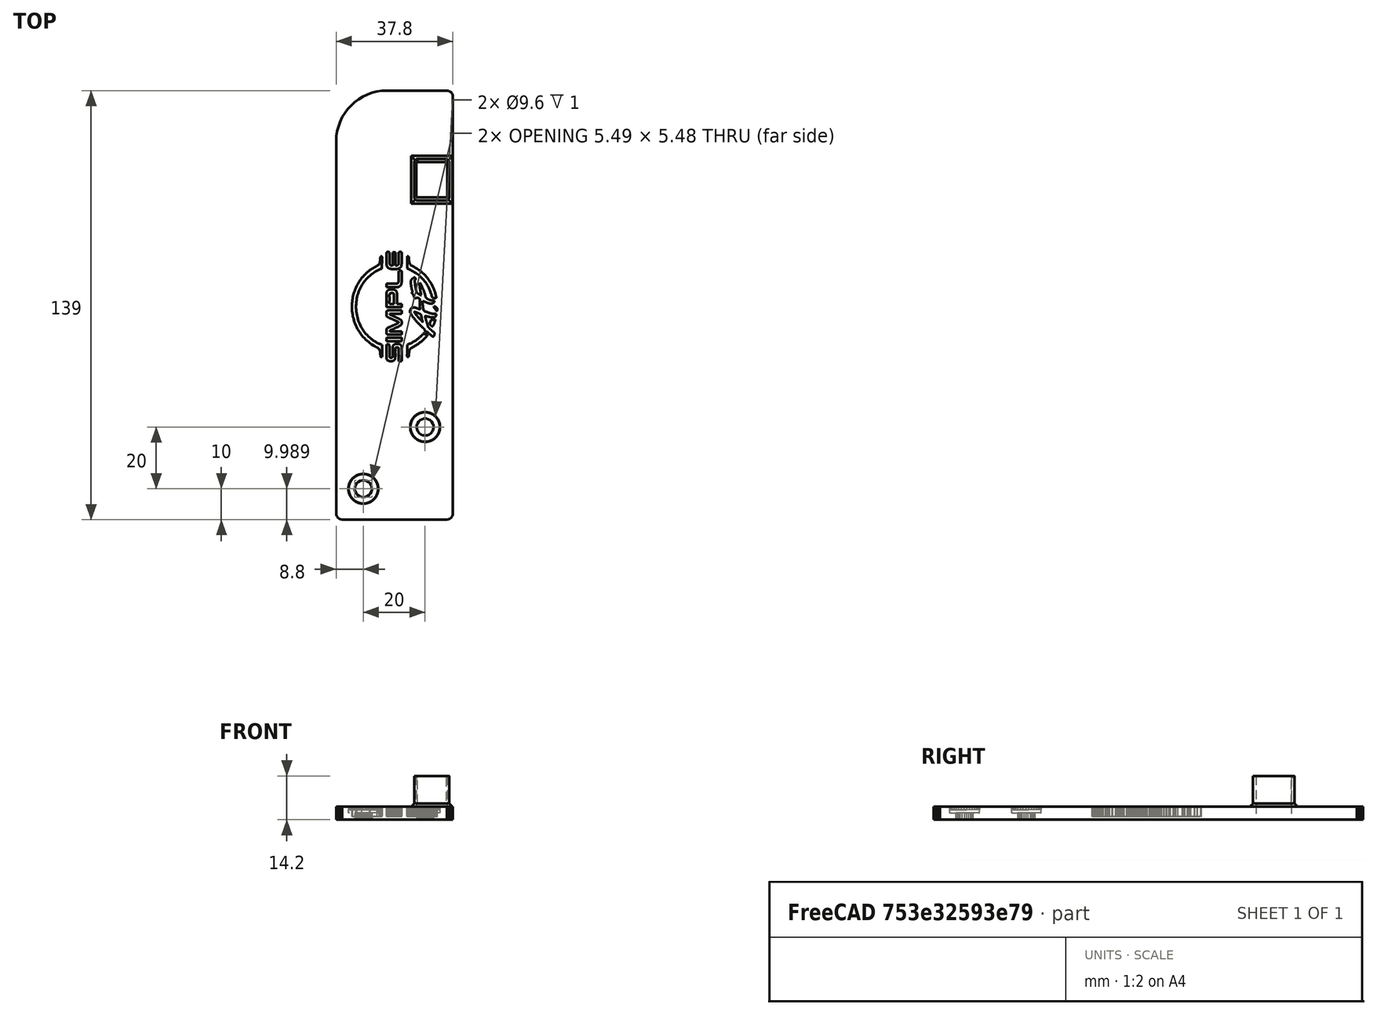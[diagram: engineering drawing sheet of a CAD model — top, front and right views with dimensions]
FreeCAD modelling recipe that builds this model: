
FCSTD DOCUMENT  (FreeCAD 1.1R44555 (Git))
Label: Ender3USBSupport
License: All rights reserved
LicenseURL: https://en.wikipedia.org/wiki/All_rights_reserved
objects: Sketcher::SketchObject×10, PartDesign::Pocket×6, PartDesign::Pad×5, PartDesign::SubShapeBinder×3, Part::Feature×2, PartDesign::Chamfer×2, Mesh::Feature×1, Part::Refine×1, App::Point×1, PartDesign::FeatureBase×1, PartDesign::Fillet×1, PartDesign::Body×1
note: 71 computed .brp shape members not serialized (recipe doc carries the construction recipe); baked Part::Feature solids carry a one-line shape summary decoded from their .brp

FEATURE [Mesh::Feature] House
FEATURE [Part::Feature] House001
  shape: bbox 37.8 x 139 x 16.2 mm, 1878 faces, 0 solids (baked)
FEATURE [Part::Refine] House002
  Source = -> House001
FEATURE [Part::Feature] House002_solid  label="House002 (Solid)"
  shape: bbox 37.8 x 139 x 16.2 mm, 936 faces (baked)
FEATURE [App::Point] Origin001
  Role = Origin
FEATURE [PartDesign::FeatureBase] BaseFeature
  BaseFeature = -> House002_solid
  Suppressed = false
FEATURE [Sketcher::SketchObject] Sketch
  ArcFitTolerance = 1e-06
  AttachmentSupport = -> [BaseFeature]
  ExternalTypes = [0]
  FullyConstrained = false
  MakeInternals = false
  MapMode = 5
  Placement = pos=(0,0,16.1903) rot=(0,0,1;0rad)
  sketch-geometry (4):
    g0: LineSegment StartX=26.4364 StartY=143.827 StartZ=0 EndX=26.4364 EndY=37.4239 EndZ=0
    g1: LineSegment StartX=26.4364 StartY=37.4239 StartZ=0 EndX=73.2674 EndY=37.4239 EndZ=0
    g2: LineSegment StartX=73.2674 StartY=37.4239 StartZ=0 EndX=73.2674 EndY=143.827 EndZ=0
    g3: LineSegment StartX=73.2674 StartY=143.827 StartZ=0 EndX=26.4364 EndY=143.827 EndZ=0
  constraints (8):
    c: Coincident(g0,g1)
    c: Coincident(g1,g2)
    c: Coincident(g2,g3)
    c: Coincident(g3,g0)
    c: Vertical(g0)
    c: Vertical(g2)
    c: Horizontal(g1)
    c: Horizontal(g3)
FEATURE [PartDesign::Pocket] Pocket
  BaseFeature = -> BaseFeature
  Direction = (0,0,-1)
  Length = 5
  Length2 = 5
  Profile = -> Sketch
  ReferenceAxis = -> Sketch [N_Axis]
  Refine = true
  SideType = 0
  Suppressed = false
  Type = 3
  Type2 = 0
  UpToFace = -> BaseFeature [Face370]
FEATURE [PartDesign::SubShapeBinder] Binder
  BindCopyOnChange = 0
  BindMode = 0
  ClaimChildren = false
  Context = -> Body [Binder.]
  Fuse = false
  MakeFace = true
  OffsetFill = false
  OffsetIntersection = false
  OffsetJoinType = 0
  OffsetOpenResult = false
  PartialLoad = false
  Refine = true
  Relative = true
  Support = -> [Pocket[Face177]]
  _Version = 2
FEATURE [PartDesign::Pad] Pad
  BaseFeature = -> Pocket
  Direction = (0,0,-1)
  Length = 10
  Length2 = 10
  Profile = -> Binder
  Refine = true
  SideType = 0
  Suppressed = false
  Type = 3
  Type2 = 0
  UpToFace = -> Pocket [Face86]
FEATURE [Sketcher::SketchObject] Sketch001
  ArcFitTolerance = 1e-06
  AttachmentSupport = -> [Pad]
  ExternalGeometry = -> [Pad]
  ExternalTypes = [0,0,0,0,0,0,0,0,0]
  FullyConstrained = false
  MakeInternals = false
  MapMode = 5
  Placement = pos=(0,0,2.19031) rot=(0,0,1;0rad)
  sketch-geometry (10):
    g0: LineSegment StartX=68.7903 StartY=103.4 StartZ=0 EndX=57.4903 EndY=103.4 EndZ=0
    g1: LineSegment StartX=57.4903 StartY=103.4 StartZ=0 EndX=57.4903 EndY=116.8 EndZ=0
    g2: LineSegment StartX=57.4903 StartY=116.8 StartZ=0 EndX=62.8903 EndY=116.8 EndZ=0
    g3: LineSegment StartX=62.8903 StartY=115.6 StartZ=0 EndX=58.6903 EndY=115.6 EndZ=0
    g4: LineSegment StartX=58.6903 StartY=115.6 StartZ=0 EndX=58.6903 EndY=104.6 EndZ=0
    g5: LineSegment StartX=58.6903 StartY=104.6 StartZ=0 EndX=66.6903 EndY=104.6 EndZ=0
    g6: LineSegment StartX=66.6903 StartY=104.6 StartZ=0 EndX=66.6903 EndY=115.6 EndZ=0
    g7: LineSegment StartX=66.6903 StartY=115.6 StartZ=0 EndX=62.8903 EndY=115.6 EndZ=0
    g8: LineSegment StartX=62.8903 StartY=116.8 StartZ=0 EndX=68.7903 EndY=116.8 EndZ=0
    g9: LineSegment StartX=68.7903 StartY=116.8 StartZ=0 EndX=68.7903 EndY=103.4 EndZ=0
  constraints (18):
    c: Coincident(g-5,g0)
    c: Coincident(g0,g-5)
    c: Coincident(g0,g1)
    c: Coincident(g1,g-11)
    c: Coincident(g1,g2)
    c: Coincident(g3,g-8)
    c: Coincident(g3,g4)
    c: Coincident(g4,g-7)
    c: Coincident(g4,g5)
    c: Coincident(g5,g-10)
    c: Coincident(g5,g6)
    c: Coincident(g6,g-10)
    c: Coincident(g6,g7)
    c: Coincident(g8,g-4)
    c: Coincident(g8,g9)
    c: Coincident(g9,g0)
    c: Coincident(g2,g8)
    c: Coincident(g3,g7)
FEATURE [PartDesign::Pad] Pad001
  BaseFeature = -> Pad
  Direction = (0,0,1)
  Length = 10
  Length2 = 10
  Profile = -> Sketch001
  ReferenceAxis = -> Sketch001 [N_Axis]
  Refine = true
  SideType = 0
  Suppressed = false
  Type = 0
  Type2 = 0
FEATURE [Sketcher::SketchObject] Sketch002
  ArcFitTolerance = 1e-06
  AttachmentSupport = -> [Pad001]
  ExternalGeometry = -> [Pad001]
  ExternalTypes = [0,0,0,0,0,0,0,0,0]
  FullyConstrained = true
  MakeInternals = false
  MapMode = 5
  Placement = pos=(0,0,2.19031) rot=(0,0,1;0rad)
  sketch-geometry (8):
    g0: LineSegment StartX=68.7903 StartY=73 StartZ=0 EndX=43.3903 EndY=73 EndZ=0
    g1: LineSegment StartX=43.3903 StartY=73 StartZ=0 EndX=43.3903 EndY=137.8 EndZ=0
    g2: LineSegment StartX=43.3903 StartY=137.8 StartZ=0 EndX=68.7903 EndY=137.8 EndZ=0
    g3: LineSegment StartX=68.7903 StartY=137.8 StartZ=0 EndX=68.7903 EndY=116.8 EndZ=0
    g4: LineSegment StartX=68.7903 StartY=116.8 StartZ=0 EndX=57.4903 EndY=116.8 EndZ=0
    g5: LineSegment StartX=57.4903 StartY=116.8 StartZ=0 EndX=57.4903 EndY=103.4 EndZ=0
    g6: LineSegment StartX=68.7903 StartY=103.4 StartZ=0 EndX=68.7903 EndY=73 EndZ=0
    g7: LineSegment StartX=57.4903 StartY=103.4 StartZ=0 EndX=68.7903 EndY=103.4 EndZ=0
  constraints (18):
    c: Coincident(g0,g-4)
    c: Horizontal(g0)
    c: Coincident(g0,g1)
    c: Coincident(g1,g-5)
    c: Vertical(g1)
    c: Coincident(g1,g2)
    c: Horizontal(g2)
    c: Coincident(g2,g3)
    c: Coincident(g3,g-11)
    c: Vertical(g3)
    c: Coincident(g3,g4)
    c: Coincident(g4,g-10)
    c: Coincident(g4,g5)
    c: Coincident(g6,g0)
    c: Coincident(g7,g-8)
    c: Coincident(g7,g-9)
    c: Coincident(g6,g7)
    c: Coincident(g5,g7)
FEATURE [PartDesign::Pad] Pad002
  BaseFeature = -> Pad001
  Direction = (0,0,1)
  Length = 10
  Length2 = 10
  Profile = -> Sketch002
  ReferenceAxis = -> Sketch002 [N_Axis]
  Refine = true
  Reversed = true
  SideType = 0
  Suppressed = false
  Type = 3
  Type2 = 0
  UpToFace = -> Pad001 [Face134]
FEATURE [PartDesign::SubShapeBinder] Binder001
  BindCopyOnChange = 0
  BindMode = 0
  ClaimChildren = false
  Context = -> Body [Binder001.]
  Fuse = false
  MakeFace = true
  OffsetFill = false
  OffsetIntersection = false
  OffsetJoinType = 0
  OffsetOpenResult = false
  PartialLoad = false
  Refine = true
  Relative = true
  Support = -> [Pad002[Face165]]
  _Version = 2
FEATURE [PartDesign::Pad] Pad003
  BaseFeature = -> Pad002
  Direction = (0,0,-1)
  Length = 10
  Length2 = 10
  Profile = -> Binder001
  Refine = true
  SideType = 0
  Suppressed = false
  Type = 3
  Type2 = 0
  UpToFace = -> Pad002 [Face125]
FEATURE [PartDesign::Chamfer] Chamfer
  Angle = 45
  Base = -> Pad003 [Edge87,Edge88,Edge86]
  BaseFeature = -> Pad003
  ChamferType = 0
  FlipDirection = false
  Refine = true
  Size = 1
  Size2 = 1
  SupportTransform = false
  Suppressed = false
  UseAllEdges = false
FEATURE [PartDesign::Chamfer] Chamfer001
  Angle = 45
  Base = -> Chamfer [Edge2]
  BaseFeature = -> Chamfer
  ChamferType = 0
  FlipDirection = false
  Refine = true
  Size = 1
  Size2 = 1
  SupportTransform = false
  Suppressed = false
  UseAllEdges = false
FEATURE [PartDesign::Fillet] Fillet
  Base = -> Chamfer001 [Edge298,Edge294,Edge300,Edge296]
  BaseFeature = -> Chamfer001
  Radius = 1
  Refine = true
  SupportTransform = false
  Suppressed = false
  UseAllEdges = false
FEATURE [Sketcher::SketchObject] Sketch003
  ArcFitTolerance = 1e-06
  AttachmentSupport = -> [Fillet]
  ExternalGeometry = -> [Fillet]
  ExternalTypes = [0,0,0,0,0]
  FullyConstrained = true
  MakeInternals = false
  MapMode = 5
  Placement = pos=(0,0,2.19031) rot=(0,0,1;0rad)
  sketch-geometry (4):
    g0: LineSegment StartX=61.4903 StartY=132.8 StartZ=0 EndX=61.4903 EndY=119.3 EndZ=0
    g1: LineSegment StartX=61.4903 StartY=119.3 StartZ=0 EndX=64.4903 EndY=119.3 EndZ=0
    g2: LineSegment StartX=64.4903 StartY=119.3 StartZ=0 EndX=64.4903 EndY=132.8 EndZ=0
    g3: LineSegment StartX=64.4903 StartY=132.8 StartZ=0 EndX=61.4903 EndY=132.8 EndZ=0
  constraints (12):
    c: Coincident(g0,g1)
    c: Coincident(g1,g2)
    c: Coincident(g2,g3)
    c: Coincident(g3,g0)
    c: Vertical(g0)
    c: Vertical(g2)
    c: Horizontal(g1)
    c: Horizontal(g3)
    c: DistanceY(g2,g2) = 13.5
    c: DistanceY(g-3,g0) = 1.5
    c: Distance(g1,g1) = 3
    c: Distance(g1,g-7) = 5.5
FEATURE [Sketcher::SketchObject] Sketch006
  ArcFitTolerance = 1e-06
  ExternalTypes = [0,0]
  FullyConstrained = false
  MakeInternals = false
  MapMode = 5
  Placement = pos=(0,0,2.19031) rot=(0,0,1;0rad)
  sketch-geometry (3):
    g0: ArcOfCircle CenterX=48.6683 CenterY=122.522 CenterZ=0 NormalX=0 NormalY=0 NormalZ=1 AngleXU=0 Radius=16.478 StartAngle=1.5708 EndAngle=3.14159
    g1: LineSegment StartX=32.1903 StartY=122.522 StartZ=0 EndX=32.083 EndY=139 EndZ=0
    g2: LineSegment StartX=32.083 StartY=139 StartZ=0 EndX=48.6683 EndY=139 EndZ=0
  constraints (6):
    c: Coincident(g0,g1)
    c: Coincident(g1,g2)
    c: Coincident(g2,g0)
    c: Horizontal(g2)
    c: Tangent(g0,g-4) = -1.5708
    c: Tangent(g0,g-3) = 1.5708
FEATURE [PartDesign::Pocket] Pocket004
  BaseFeature = -> Fillet
  Direction = (0,0,-1)
  Length = 5
  Length2 = 5
  Profile = -> Sketch006
  ReferenceAxis = -> Sketch006 [N_Axis]
  Refine = true
  SideType = 0
  Suppressed = false
  Type = 0
  Type2 = 0
FEATURE [PartDesign::SubShapeBinder] Binder002
  BindCopyOnChange = 0
  BindMode = 0
  ClaimChildren = false
  Context = -> Body [Binder002.]
  Fuse = false
  MakeFace = true
  OffsetFill = false
  OffsetIntersection = false
  OffsetJoinType = 0
  OffsetOpenResult = false
  PartialLoad = false
  Refine = true
  Relative = true
  Support = -> [Pocket004[Face108]]
  _Version = 2
FEATURE [PartDesign::Pad] Pad004
  BaseFeature = -> Pocket004
  Direction = (0,0,-1)
  Length = 2
  Length2 = 10
  Profile = -> Binder002
  Refine = true
  SideType = 0
  Suppressed = false
  Type = 0
  Type2 = 0
FEATURE [Sketcher::SketchObject] Sketch004
  ArcFitTolerance = 1e-06
  AttachmentOffset = pos=(37,87,0) rot=(0,0,1;0rad)
  AttachmentSupport = -> [Pad004]
  ExternalTypes = [0]
  FullyConstrained = false
  MakeInternals = false
  MapMode = 5
  Placement = pos=(37,87,2.19031) rot=(0,0,1;0rad)
  sketch-geometry (160):
    g0: BSplineCurve PolesCount=4 KnotsCount=2 Degree=3 IsPeriodic=0
    g1: BSplineCurve PolesCount=4 KnotsCount=2 Degree=3 IsPeriodic=0
    g2: BSplineCurve PolesCount=4 KnotsCount=2 Degree=3 IsPeriodic=0
    g3: BSplineCurve PolesCount=4 KnotsCount=2 Degree=3 IsPeriodic=0
    g4: BSplineCurve PolesCount=4 KnotsCount=2 Degree=3 IsPeriodic=0
    g5: BSplineCurve PolesCount=4 KnotsCount=2 Degree=3 IsPeriodic=0
    g6: BSplineCurve PolesCount=4 KnotsCount=2 Degree=3 IsPeriodic=0
    g7: BSplineCurve PolesCount=4 KnotsCount=2 Degree=3 IsPeriodic=0
    g8: BSplineCurve PolesCount=4 KnotsCount=2 Degree=3 IsPeriodic=0
    g9: BSplineCurve PolesCount=4 KnotsCount=2 Degree=3 IsPeriodic=0
    g10: BSplineCurve PolesCount=4 KnotsCount=2 Degree=3 IsPeriodic=0
    g11: BSplineCurve PolesCount=4 KnotsCount=2 Degree=3 IsPeriodic=0
    g12: BSplineCurve PolesCount=4 KnotsCount=2 Degree=3 IsPeriodic=0
    g13: BSplineCurve PolesCount=4 KnotsCount=2 Degree=3 IsPeriodic=0
    g14: BSplineCurve PolesCount=4 KnotsCount=2 Degree=3 IsPeriodic=0
    g15: BSplineCurve PolesCount=4 KnotsCount=2 Degree=3 IsPeriodic=0
    g16: BSplineCurve PolesCount=4 KnotsCount=2 Degree=3 IsPeriodic=0
    g17: BSplineCurve PolesCount=4 KnotsCount=2 Degree=3 IsPeriodic=0
    g18: BSplineCurve PolesCount=4 KnotsCount=2 Degree=3 IsPeriodic=0
    g19: BSplineCurve PolesCount=4 KnotsCount=2 Degree=3 IsPeriodic=0
    g20: BSplineCurve PolesCount=4 KnotsCount=2 Degree=3 IsPeriodic=0
    g21: BSplineCurve PolesCount=4 KnotsCount=2 Degree=3 IsPeriodic=0
    g22: BSplineCurve PolesCount=4 KnotsCount=2 Degree=3 IsPeriodic=0
    g23: BSplineCurve PolesCount=4 KnotsCount=2 Degree=3 IsPeriodic=0
    g24: BSplineCurve PolesCount=4 KnotsCount=2 Degree=3 IsPeriodic=0
    g25: BSplineCurve PolesCount=4 KnotsCount=2 Degree=3 IsPeriodic=0
    g26: BSplineCurve PolesCount=4 KnotsCount=2 Degree=3 IsPeriodic=0
    g27: BSplineCurve PolesCount=4 KnotsCount=2 Degree=3 IsPeriodic=0
    g28: BSplineCurve PolesCount=4 KnotsCount=2 Degree=3 IsPeriodic=0
    g29: BSplineCurve PolesCount=4 KnotsCount=2 Degree=3 IsPeriodic=0
    g30: BSplineCurve PolesCount=4 KnotsCount=2 Degree=3 IsPeriodic=0
    g31: BSplineCurve PolesCount=4 KnotsCount=2 Degree=3 IsPeriodic=0
    g32: BSplineCurve PolesCount=4 KnotsCount=2 Degree=3 IsPeriodic=0
    g33: BSplineCurve PolesCount=4 KnotsCount=2 Degree=3 IsPeriodic=0
    g34: BSplineCurve PolesCount=4 KnotsCount=2 Degree=3 IsPeriodic=0
    g35: BSplineCurve PolesCount=4 KnotsCount=2 Degree=3 IsPeriodic=0
    g36: BSplineCurve PolesCount=4 KnotsCount=2 Degree=3 IsPeriodic=0
    g37: BSplineCurve PolesCount=4 KnotsCount=2 Degree=3 IsPeriodic=0
    g38: BSplineCurve PolesCount=4 KnotsCount=2 Degree=3 IsPeriodic=0
    g39: BSplineCurve PolesCount=4 KnotsCount=2 Degree=3 IsPeriodic=0
    g40: BSplineCurve PolesCount=4 KnotsCount=2 Degree=3 IsPeriodic=0
    g41: BSplineCurve PolesCount=4 KnotsCount=2 Degree=3 IsPeriodic=0
    g42: BSplineCurve PolesCount=4 KnotsCount=2 Degree=3 IsPeriodic=0
    g43: BSplineCurve PolesCount=4 KnotsCount=2 Degree=3 IsPeriodic=0
    g44: BSplineCurve PolesCount=4 KnotsCount=2 Degree=3 IsPeriodic=0
    g45: BSplineCurve PolesCount=4 KnotsCount=2 Degree=3 IsPeriodic=0
    g46: BSplineCurve PolesCount=4 KnotsCount=2 Degree=3 IsPeriodic=0
    g47: BSplineCurve PolesCount=4 KnotsCount=2 Degree=3 IsPeriodic=0
    g48: BSplineCurve PolesCount=4 KnotsCount=2 Degree=3 IsPeriodic=0
    g49: BSplineCurve PolesCount=4 KnotsCount=2 Degree=3 IsPeriodic=0
    g50: BSplineCurve PolesCount=4 KnotsCount=2 Degree=3 IsPeriodic=0
    g51: BSplineCurve PolesCount=4 KnotsCount=2 Degree=3 IsPeriodic=0
    g52: BSplineCurve PolesCount=4 KnotsCount=2 Degree=3 IsPeriodic=0
    g53: BSplineCurve PolesCount=4 KnotsCount=2 Degree=3 IsPeriodic=0
    g54: BSplineCurve PolesCount=4 KnotsCount=2 Degree=3 IsPeriodic=0
    g55: BSplineCurve PolesCount=4 KnotsCount=2 Degree=3 IsPeriodic=0
    g56: BSplineCurve PolesCount=4 KnotsCount=2 Degree=3 IsPeriodic=0
    g57: BSplineCurve PolesCount=4 KnotsCount=2 Degree=3 IsPeriodic=0
    g58: BSplineCurve PolesCount=4 KnotsCount=2 Degree=3 IsPeriodic=0
    g59: BSplineCurve PolesCount=4 KnotsCount=2 Degree=3 IsPeriodic=0
    g60: BSplineCurve PolesCount=4 KnotsCount=2 Degree=3 IsPeriodic=0
    g61: BSplineCurve PolesCount=4 KnotsCount=2 Degree=3 IsPeriodic=0
    g62: BSplineCurve PolesCount=4 KnotsCount=2 Degree=3 IsPeriodic=0
    g63: BSplineCurve PolesCount=4 KnotsCount=2 Degree=3 IsPeriodic=0
    g64: BSplineCurve PolesCount=4 KnotsCount=2 Degree=3 IsPeriodic=0
    g65: BSplineCurve PolesCount=4 KnotsCount=2 Degree=3 IsPeriodic=0
    g66: BSplineCurve PolesCount=4 KnotsCount=2 Degree=3 IsPeriodic=0
    g67: BSplineCurve PolesCount=4 KnotsCount=2 Degree=3 IsPeriodic=0
    g68: BSplineCurve PolesCount=4 KnotsCount=2 Degree=3 IsPeriodic=0
    g69: BSplineCurve PolesCount=4 KnotsCount=2 Degree=3 IsPeriodic=0
    g70: BSplineCurve PolesCount=4 KnotsCount=2 Degree=3 IsPeriodic=0
    g71: BSplineCurve PolesCount=4 KnotsCount=2 Degree=3 IsPeriodic=0
    g72: BSplineCurve PolesCount=4 KnotsCount=2 Degree=3 IsPeriodic=0
    g73: BSplineCurve PolesCount=4 KnotsCount=2 Degree=3 IsPeriodic=0
    g74: BSplineCurve PolesCount=4 KnotsCount=2 Degree=3 IsPeriodic=0
    g75: BSplineCurve PolesCount=4 KnotsCount=2 Degree=3 IsPeriodic=0
    g76: BSplineCurve PolesCount=4 KnotsCount=2 Degree=3 IsPeriodic=0
    g77: BSplineCurve PolesCount=4 KnotsCount=2 Degree=3 IsPeriodic=0
    g78: BSplineCurve PolesCount=4 KnotsCount=2 Degree=3 IsPeriodic=0
    g79: BSplineCurve PolesCount=4 KnotsCount=2 Degree=3 IsPeriodic=0
    g80: BSplineCurve PolesCount=4 KnotsCount=2 Degree=3 IsPeriodic=0
    g81: BSplineCurve PolesCount=4 KnotsCount=2 Degree=3 IsPeriodic=0
    g82: BSplineCurve PolesCount=4 KnotsCount=2 Degree=3 IsPeriodic=0
    g83: BSplineCurve PolesCount=4 KnotsCount=2 Degree=3 IsPeriodic=0
    g84: BSplineCurve PolesCount=4 KnotsCount=2 Degree=3 IsPeriodic=0
    g85: BSplineCurve PolesCount=4 KnotsCount=2 Degree=3 IsPeriodic=0
    g86: BSplineCurve PolesCount=4 KnotsCount=2 Degree=3 IsPeriodic=0
    g87: BSplineCurve PolesCount=4 KnotsCount=2 Degree=3 IsPeriodic=0
    g88: BSplineCurve PolesCount=4 KnotsCount=2 Degree=3 IsPeriodic=0
    g89: BSplineCurve PolesCount=4 KnotsCount=2 Degree=3 IsPeriodic=0
    g90: BSplineCurve PolesCount=4 KnotsCount=2 Degree=3 IsPeriodic=0
    g91: BSplineCurve PolesCount=4 KnotsCount=2 Degree=3 IsPeriodic=0
    g92: BSplineCurve PolesCount=4 KnotsCount=2 Degree=3 IsPeriodic=0
    g93: BSplineCurve PolesCount=4 KnotsCount=2 Degree=3 IsPeriodic=0
    g94: BSplineCurve PolesCount=4 KnotsCount=2 Degree=3 IsPeriodic=0
    g95: BSplineCurve PolesCount=4 KnotsCount=2 Degree=3 IsPeriodic=0
    g96: BSplineCurve PolesCount=4 KnotsCount=2 Degree=3 IsPeriodic=0
    g97: BSplineCurve PolesCount=4 KnotsCount=2 Degree=3 IsPeriodic=0
    g98: BSplineCurve PolesCount=4 KnotsCount=2 Degree=3 IsPeriodic=0
    g99: BSplineCurve PolesCount=4 KnotsCount=2 Degree=3 IsPeriodic=0
    g100: BSplineCurve PolesCount=4 KnotsCount=2 Degree=3 IsPeriodic=0
    g101: BSplineCurve PolesCount=4 KnotsCount=2 Degree=3 IsPeriodic=0
    g102: BSplineCurve PolesCount=4 KnotsCount=2 Degree=3 IsPeriodic=0
    g103: BSplineCurve PolesCount=4 KnotsCount=2 Degree=3 IsPeriodic=0
    g104: BSplineCurve PolesCount=4 KnotsCount=2 Degree=3 IsPeriodic=0
    g105: BSplineCurve PolesCount=2 KnotsCount=2 Degree=1 IsPeriodic=0
    g106: BSplineCurve PolesCount=4 KnotsCount=2 Degree=3 IsPeriodic=0
    g107: BSplineCurve PolesCount=4 KnotsCount=2 Degree=3 IsPeriodic=0
    g108: BSplineCurve PolesCount=4 KnotsCount=2 Degree=3 IsPeriodic=0
    g109: BSplineCurve PolesCount=4 KnotsCount=2 Degree=3 IsPeriodic=0
    g110: BSplineCurve PolesCount=4 KnotsCount=2 Degree=3 IsPeriodic=0
    g111: BSplineCurve PolesCount=4 KnotsCount=2 Degree=3 IsPeriodic=0
    g112: BSplineCurve PolesCount=4 KnotsCount=2 Degree=3 IsPeriodic=0
    g113: BSplineCurve PolesCount=4 KnotsCount=2 Degree=3 IsPeriodic=0
    g114: BSplineCurve PolesCount=4 KnotsCount=2 Degree=3 IsPeriodic=0
    g115: BSplineCurve PolesCount=4 KnotsCount=2 Degree=3 IsPeriodic=0
    g116: BSplineCurve PolesCount=4 KnotsCount=2 Degree=3 IsPeriodic=0
    g117: BSplineCurve PolesCount=4 KnotsCount=2 Degree=3 IsPeriodic=0
    g118: BSplineCurve PolesCount=4 KnotsCount=2 Degree=3 IsPeriodic=0
    g119: BSplineCurve PolesCount=4 KnotsCount=2 Degree=3 IsPeriodic=0
    g120: BSplineCurve PolesCount=4 KnotsCount=2 Degree=3 IsPeriodic=0
    g121: BSplineCurve PolesCount=4 KnotsCount=2 Degree=3 IsPeriodic=0
    g122: BSplineCurve PolesCount=4 KnotsCount=2 Degree=3 IsPeriodic=0
    g123: BSplineCurve PolesCount=4 KnotsCount=2 Degree=3 IsPeriodic=0
    g124: BSplineCurve PolesCount=4 KnotsCount=2 Degree=3 IsPeriodic=0
    g125: BSplineCurve PolesCount=4 KnotsCount=2 Degree=3 IsPeriodic=0
    g126: BSplineCurve PolesCount=4 KnotsCount=2 Degree=3 IsPeriodic=0
    g127: BSplineCurve PolesCount=4 KnotsCount=2 Degree=3 IsPeriodic=0
    g128: BSplineCurve PolesCount=4 KnotsCount=2 Degree=3 IsPeriodic=0
    g129: BSplineCurve PolesCount=4 KnotsCount=2 Degree=3 IsPeriodic=0
    g130: BSplineCurve PolesCount=4 KnotsCount=2 Degree=3 IsPeriodic=0
    g131: BSplineCurve PolesCount=4 KnotsCount=2 Degree=3 IsPeriodic=0
    g132: BSplineCurve PolesCount=4 KnotsCount=2 Degree=3 IsPeriodic=0
    g133: BSplineCurve PolesCount=4 KnotsCount=2 Degree=3 IsPeriodic=0
    g134: BSplineCurve PolesCount=4 KnotsCount=2 Degree=3 IsPeriodic=0
    g135: BSplineCurve PolesCount=4 KnotsCount=2 Degree=3 IsPeriodic=0
    g136: BSplineCurve PolesCount=4 KnotsCount=2 Degree=3 IsPeriodic=0
    g137: BSplineCurve PolesCount=4 KnotsCount=2 Degree=3 IsPeriodic=0
    g138: BSplineCurve PolesCount=4 KnotsCount=2 Degree=3 IsPeriodic=0
    g139: BSplineCurve PolesCount=4 KnotsCount=2 Degree=3 IsPeriodic=0
    g140: BSplineCurve PolesCount=4 KnotsCount=2 Degree=3 IsPeriodic=0
    g141: BSplineCurve PolesCount=4 KnotsCount=2 Degree=3 IsPeriodic=0
    g142: BSplineCurve PolesCount=4 KnotsCount=2 Degree=3 IsPeriodic=0
    g143: BSplineCurve PolesCount=4 KnotsCount=2 Degree=3 IsPeriodic=0
    g144: BSplineCurve PolesCount=4 KnotsCount=2 Degree=3 IsPeriodic=0
    g145: BSplineCurve PolesCount=4 KnotsCount=2 Degree=3 IsPeriodic=0
    g146: BSplineCurve PolesCount=4 KnotsCount=2 Degree=3 IsPeriodic=0
    g147: BSplineCurve PolesCount=4 KnotsCount=2 Degree=3 IsPeriodic=0
    g148: BSplineCurve PolesCount=4 KnotsCount=2 Degree=3 IsPeriodic=0
    g149: BSplineCurve PolesCount=4 KnotsCount=2 Degree=3 IsPeriodic=0
    g150: BSplineCurve PolesCount=4 KnotsCount=2 Degree=3 IsPeriodic=0
    g151: BSplineCurve PolesCount=4 KnotsCount=2 Degree=3 IsPeriodic=0
    g152: BSplineCurve PolesCount=4 KnotsCount=2 Degree=3 IsPeriodic=0
    g153: BSplineCurve PolesCount=4 KnotsCount=2 Degree=3 IsPeriodic=0
    g154: BSplineCurve PolesCount=4 KnotsCount=2 Degree=3 IsPeriodic=0
    g155: BSplineCurve PolesCount=4 KnotsCount=2 Degree=3 IsPeriodic=0
    g156: BSplineCurve PolesCount=4 KnotsCount=2 Degree=3 IsPeriodic=0
    g157: BSplineCurve PolesCount=4 KnotsCount=2 Degree=3 IsPeriodic=0
    g158: BSplineCurve PolesCount=4 KnotsCount=2 Degree=3 IsPeriodic=0
    g159: BSplineCurve PolesCount=4 KnotsCount=2 Degree=3 IsPeriodic=0
  constraints (160):
    c: Coincident(g10,g11)
    c: Coincident(g4,g5)
    c: Coincident(g11,g12)
    c: Coincident(g0,g12)
    c: Coincident(g5,g6)
    c: Coincident(g9,g10)
    c: Coincident(g0,g1)
    c: Coincident(g8,g9)
    c: Coincident(g1,g2)
    c: Coincident(g3,g4)
    c: Coincident(g2,g3)
    c: Coincident(g7,g8)
    c: Coincident(g6,g7)
    c: Coincident(g79,g80)
    c: Coincident(g96,g97)
    c: Coincident(g109,g110)
    c: Coincident(g13,g26)
    c: Coincident(g110,g111)
    c: Coincident(g13,g14)
    c: Coincident(g136,g137)
    c: Coincident(g102,g103)
    c: Coincident(g82,g83)
    c: Coincident(g137,g138)
    c: Coincident(g103,g104)
    c: Coincident(g78,g79)
    c: Coincident(g83,g84)
    c: Coincident(g80,g81)
    c: Coincident(g25,g26)
    c: Coincident(g95,g96)
    c: Coincident(g108,g109)
    c: Coincident(g73,g81)
    c: Coincident(g14,g15)
    c: Coincident(g111,g112)
    c: Coincident(g127,g131)
    c: Coincident(g127,g128)
    c: Coincident(g87,g88)
    c: Coincident(g91,g92)
    c: Coincident(g112,g113)
    c: Coincident(g15,g16)
    c: Coincident(g130,g131)
    c: Coincident(g97,g98)
    c: Coincident(g88,g89)
    c: Coincident(g84,g85)
    c: Coincident(g92,g93)
    c: Coincident(g113,g114)
    c: Coincident(g16,g17)
    c: Coincident(g17,g18)
    c: Coincident(g114,g115)
    c: Coincident(g82,g100)
    c: Coincident(g129,g130)
    c: Coincident(g128,g129)
    c: Coincident(g73,g74)
    c: Coincident(g107,g108)
    c: Coincident(g135,g136)
    c: Coincident(g18,g19)
    c: Coincident(g19,g20)
    c: Coincident(g106,g107)
    c: Coincident(g24,g25)
    c: Coincident(g99,g100)
    c: Coincident(g106,g120)
    c: Coincident(g74,g75)
    c: Coincident(g75,g76)
    c: Coincident(g138,g139)
    c: Coincident(g119,g120)
    c: Coincident(g139,g140)
    c: Coincident(g132,g140)
    c: Coincident(g20,g21)
    c: Coincident(g98,g99)
    c: Coincident(g118,g119)
    c: Coincident(g132,g133)
    c: Coincident(g21,g22)
    c: Coincident(g115,g116)
    c: Coincident(g90,g91)
    c: Coincident(g89,g90)
    c: Coincident(g77,g78)
    c: Coincident(g134,g135)
    c: Coincident(g85,g86)
    c: Coincident(g86,g87)
    c: Coincident(g23,g24)
    c: Coincident(g104,g105)
    c: Coincident(g101,g102)
    c: Coincident(g94,g95)
    c: Coincident(g117,g118)
    c: Coincident(g101,g105)
    c: Coincident(g22,g23)
    c: Coincident(g93,g94)
    c: Coincident(g76,g77)
    c: Coincident(g133,g134)
    c: Coincident(g116,g117)
    c: Coincident(g148,g149)
    c: Coincident(g157,g158)
    c: Coincident(g158,g159)
    c: Coincident(g147,g148)
    c: Coincident(g146,g147)
    c: Coincident(g156,g157)
    c: Coincident(g149,g150)
    c: Coincident(g57,g58)
    c: Coincident(g155,g156)
    c: Coincident(g46,g47)
    c: Coincident(g56,g57)
    c: Coincident(g47,g48)
    c: Coincident(g48,g49)
    c: Coincident(g45,g46)
    c: Coincident(g150,g151)
    c: Coincident(g55,g56)
    c: Coincident(g49,g50)
    c: Coincident(g122,g123)
    c: Coincident(g43,g44)
    c: Coincident(g44,g45)
    c: Coincident(g54,g55)
    c: Coincident(g123,g124)
    c: Coincident(g42,g43)
    c: Coincident(g50,g51)
    c: Coincident(g124,g125)
    c: Coincident(g53,g54)
    c: Coincident(g40,g41)
    c: Coincident(g52,g53)
    c: Coincident(g51,g52)
    c: Coincident(g58,g59)
    c: Coincident(g121,g122)
    c: Coincident(g39,g40)
    c: Coincident(g41,g42)
    c: Coincident(g38,g39)
    c: Coincident(g125,g126)
    c: Coincident(g121,g126)
    c: Coincident(g32,g33)
    c: Coincident(g31,g32)
    c: Coincident(g153,g159)
    c: Coincident(g37,g38)
    c: Coincident(g59,g60)
    c: Coincident(g67,g68)
    c: Coincident(g154,g155)
    c: Coincident(g66,g67)
    c: Coincident(g36,g37)
    c: Coincident(g60,g61)
    c: Coincident(g153,g154)
    c: Coincident(g65,g66)
    c: Coincident(g68,g69)
    c: Coincident(g71,g72)
    c: Coincident(g141,g144)
    c: Coincident(g33,g34)
    c: Coincident(g64,g65)
    c: Coincident(g145,g146)
    c: Coincident(g141,g142)
    c: Coincident(g63,g64)
    c: Coincident(g145,g152)
    c: Coincident(g143,g144)
    c: Coincident(g61,g62)
    c: Coincident(g34,g35)
    c: Coincident(g29,g30)
    c: Coincident(g35,g36)
    c: Coincident(g62,g63)
    c: Coincident(g27,g30)
    c: Coincident(g69,g70)
    c: Coincident(g70,g71)
    c: Coincident(g142,g143)
    c: Coincident(g28,g29)
    c: Coincident(g151,g152)
    c: Coincident(g27,g28)
    c: Coincident(g31,g72)
FEATURE [Sketcher::SketchObject] Sketch005
  ArcFitTolerance = 1e-06
  AttachmentSupport = -> [Pad004]
  ExternalGeometry = -> [Sketch003]
  ExternalTypes = [0,0,0,0]
  FullyConstrained = true
  MakeInternals = false
  MapMode = 5
  Placement = pos=(0,0,2.19031) rot=(0,0,1;0rad)
  sketch-geometry (4):
    g0: LineSegment StartX=57.4903 StartY=133.8 StartZ=0 EndX=57.4903 EndY=118.3 EndZ=0
    g1: LineSegment StartX=57.4903 StartY=118.3 StartZ=0 EndX=68.7903 EndY=118.3 EndZ=0
    g2: LineSegment StartX=68.7903 StartY=118.3 StartZ=0 EndX=68.7903 EndY=133.8 EndZ=0
    g3: LineSegment StartX=68.7903 StartY=133.8 StartZ=0 EndX=57.4903 EndY=133.8 EndZ=0
  constraints (12):
    c: Coincident(g0,g1)
    c: Coincident(g1,g2)
    c: Coincident(g2,g3)
    c: Coincident(g3,g0)
    c: Vertical(g0)
    c: Vertical(g2)
    c: Horizontal(g1)
    c: Horizontal(g3)
    c: DistanceY(g2,g2) = 15.5
    c: DistanceY(g1,g-5) = 1
    c: DistanceX(g-4,g0) = 1
    c: DistanceX(g1,g-4) = 1
FEATURE [PartDesign::Pocket] Pocket006
  BaseFeature = -> Pad004
  Direction = (0,0,-1)
  Length = 3.2
  Length2 = 5
  Profile = -> Sketch004
  ReferenceAxis = -> Sketch004 [N_Axis]
  Refine = true
  SideType = 0
  Suppressed = false
  Type = 0
  Type2 = 0
FEATURE [Sketcher::SketchObject] Sketch007
  ArcFitTolerance = 1e-06
  AttachmentSupport = -> [Pocket006]
  ExternalGeometry = -> [Pocket006]
  ExternalTypes = [0,0,0,0,0,0]
  FullyConstrained = true
  MakeInternals = false
  MapMode = 5
  Placement = pos=(0,0,1.19031) rot=(0,0,1;0rad)
  sketch-geometry (2):
    g0: Circle CenterX=40.9903 CenterY=10 CenterZ=0 NormalX=0 NormalY=0 NormalZ=1 AngleXU=0 Radius=4.8
    g1: Circle CenterX=60.9903 CenterY=30 CenterZ=0 NormalX=0 NormalY=0 NormalZ=1 AngleXU=0 Radius=4.8
  constraints (6):
    c: PointOnObject(g-6,g0)
    c: PointOnObject(g-7,g0)
    c: PointOnObject(g-8,g0)
    c: PointOnObject(g-5,g1)
    c: PointOnObject(g-3,g1)
    c: PointOnObject(g-4,g1)
FEATURE [PartDesign::Pocket] Pocket007
  BaseFeature = -> Pocket006
  Direction = (0,0,-1)
  Length = 1
  Length2 = 5
  Profile = -> Sketch007
  ReferenceAxis = -> Sketch007 [N_Axis]
  Refine = true
  SideType = 0
  Suppressed = false
  Type = 0
  Type2 = 0
FEATURE [Sketcher::SketchObject] Sketch008
  ArcFitTolerance = 1e-06
  ExternalTypes = [0,0,0,0]
  FullyConstrained = true
  MakeInternals = false
  MapMode = 5
  Placement = pos=(0,0,12.1903) rot=(0,0,1;0rad)
  sketch-geometry (4):
    g0: LineSegment StartX=58.1903 StartY=115.8 StartZ=0 EndX=58.1903 EndY=104.4 EndZ=0
    g1: LineSegment StartX=58.1903 StartY=104.4 StartZ=0 EndX=68.1903 EndY=104.4 EndZ=0
    g2: LineSegment StartX=68.1903 StartY=104.4 StartZ=0 EndX=68.1903 EndY=115.8 EndZ=0
    g3: LineSegment StartX=68.1903 StartY=115.8 StartZ=0 EndX=58.1903 EndY=115.8 EndZ=0
  constraints (12):
    c: Coincident(g0,g1)
    c: Coincident(g1,g2)
    c: Coincident(g2,g3)
    c: Coincident(g3,g0)
    c: Vertical(g0)
    c: Vertical(g2)
    c: Horizontal(g1)
    c: Horizontal(g3)
    c: DistanceX(g1,g1) = 10
    c: DistanceY(g2,g-3) = 1
    c: DistanceY(g-4,g1) = 1
    c: Distance(g1,g-5) = 0.6
FEATURE [PartDesign::Pocket] Pocket008
  BaseFeature = -> Pocket007
  Direction = (0,0,-1)
  Length = 5
  Length2 = 5
  Profile = -> Sketch008
  ReferenceAxis = -> Sketch008 [N_Axis]
  Refine = true
  SideType = 0
  Suppressed = false
  Type = 1
  Type2 = 0
FEATURE [Sketcher::SketchObject] Sketch009
  ArcFitTolerance = 1e-06
  AttachmentSupport = -> [Pocket008]
  ExternalGeometry = -> [Pocket008]
  ExternalTypes = [0,0,0,0,0,0]
  FullyConstrained = false
  MakeInternals = false
  MapMode = 5
  Placement = pos=(0,116.8,-1.031e-13) rot=(0,0.707107,0.707107;3.14159rad)
  sketch-geometry (6):
    g0: LineSegment StartX=-67.7903 StartY=11.6925 StartZ=0 EndX=-67.7903 EndY=3.19031 EndZ=0
    g1: LineSegment StartX=-67.7903 StartY=3.19031 StartZ=0 EndX=-58.4903 EndY=3.19031 EndZ=0
    g2: LineSegment StartX=-58.4903 StartY=3.19031 StartZ=0 EndX=-58.4903 EndY=11.6379 EndZ=0
    g3: LineSegment StartX=-58.1903 StartY=12.1903 StartZ=0 EndX=-58.4903 EndY=11.6379 EndZ=0
    g4: LineSegment StartX=-68.1903 StartY=12.1903 StartZ=0 EndX=-67.7903 EndY=11.6925 EndZ=0
    g5: LineSegment StartX=-68.1903 StartY=12.1903 StartZ=0 EndX=-58.1903 EndY=12.1903 EndZ=0
  constraints (8):
    c: Coincident(g0,g1)
    c: Horizontal(g1)
    c: Vertical(g0)
    c: Coincident(g4,g-5)
    c: Coincident(g4,g0)
    c: Coincident(g5,g4)
    c: Coincident(g5,g3)
    c: Horizontal(g5)
FEATURE [PartDesign::Pocket] Pocket009
  BaseFeature = -> Pocket008
  Direction = (0,-1,2e-16)
  Length = 5
  Length2 = 5
  Profile = -> Sketch009
  ReferenceAxis = -> Sketch009 [N_Axis]
  Refine = true
  SideType = 0
  Suppressed = false
  Type = 0
  Type2 = 0
FEATURE [PartDesign::Body] Body
  AllowCompound = true
  BaseFeature = -> House002_solid
  Group = -> [BaseFeature,Sketch,Pocket,Binder,Pad,Sketch001,Pad001,Sketch002,Pad002,Binder001,Pad003,Chamfer,Chamfer001,Fillet,Sketch003,Sketch004,Sketch005,Sketch006,Pocket004,Binder002,Pad004,Pocket006,Sketch007,Pocket007,Sketch008,Pocket008,Sketch009,Pocket009]
  Origin = -> Origin
  Tip = -> Pocket009
